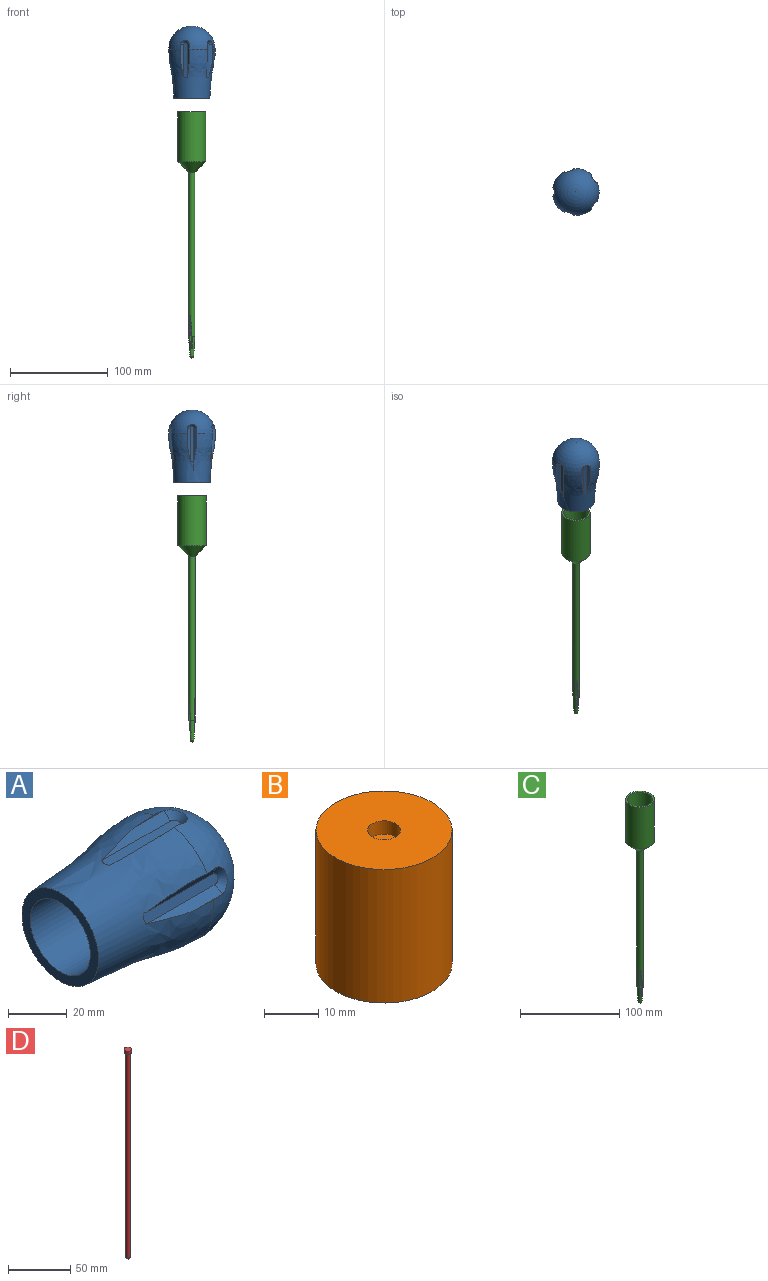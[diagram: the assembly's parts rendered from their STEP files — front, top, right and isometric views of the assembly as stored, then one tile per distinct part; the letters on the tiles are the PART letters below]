
ASSEMBLY  parts=4 mates=3
PART A: 37 faces, bbox 74.1x48.1x48.1 mm
  f0: sphere r=24mm, area 3201.7mm2, adj f1,f6,f7,f8,f9,f10,f12,f13
  f1: revolved ~50x47.78mm, area 5491.9mm2, adj f0,f2,f5,f6,f7,f8,f10,f11
  f2: plane 37x37mm, normal (-1,0,0), area 414.7mm2, adj f1,f3
  f3: cylinder r=14.5mm len=50mm, axis (1,0,0), area 4555.3mm2, adj f2,f4
  f4: plane 29x29mm, normal (-1,0,0), area 169.6mm2, adj f3,f35
  f5: plane 35.69x4.01mm, normal (0,0,1), area 140.2mm2, adj f1,f8,f9,f10
  f6: plane 14.59x0.53mm, normal (0,-1,0), area 4.7mm2, adj f0,f1,f8
  f7: plane 14.59x0.53mm, normal (0,1,0), area 4.7mm2, adj f0,f1,f10
  f8: plane 33.04x3mm, normal (0,-0.71,0.71), area 103.7mm2, adj f0,f1,f5,f6,f9
  f9: cone r=5mm half-angle=45deg, axis (0,0,1), area 35.1mm2, adj f0,f5,f8,f10
  f10: plane 33.04x3mm, normal (0,0.71,0.71), area 103.7mm2, adj f0,f1,f5,f7,f9
  f11: plane 35.69x3.81mm, normal (0,-0.95,0.31), area 140.2mm2, adj f1,f14,f15,f16
  f12: plane 14.59x0.5mm, normal (0,-0.31,-0.95), area 4.7mm2, adj f0,f1,f14
  f13: plane 14.59x0.5mm, normal (0,0.31,0.95), area 4.7mm2, adj f0,f1,f16
  f14: plane 33.04x3.78mm, normal (0,-0.89,-0.45), area 103.7mm2, adj f0,f1,f11,f12,f15
  f15: cone r=5mm half-angle=45deg, axis (0,-0.95,0.31), area 35.1mm2, adj f0,f11,f14,f16
  f16: plane 33.04x3.78mm, normal (0,-0.45,0.89), area 103.7mm2, adj f0,f1,f11,f13,f15
  f17: plane 35.69x3.24mm, normal (0,-0.59,-0.81), area 140.2mm2, adj f1,f20,f21,f22
  f18: plane 14.59x0.44mm, normal (0,0.81,-0.59), area 4.7mm2, adj f0,f1,f20
  f19: plane 14.59x0.44mm, normal (0,-0.81,0.59), area 4.7mm2, adj f0,f1,f22
  f20: plane 33.04x4.19mm, normal (0,0.16,-0.99), area 103.7mm2, adj f0,f1,f17,f18,f21
  f21: cone r=5mm half-angle=45deg, axis (0,-0.59,-0.81), area 35.1mm2, adj f0,f17,f20,f22
  f22: plane 33.04x4.19mm, normal (0,-0.99,-0.16), area 103.7mm2, adj f0,f1,f17,f19,f21
  f23: plane 35.69x3.24mm, normal (0,0.59,-0.81), area 140.2mm2, adj f1,f26,f27,f28
  f24: plane 14.59x0.44mm, normal (0,0.81,0.59), area 4.7mm2, adj f0,f1,f26
  f25: plane 14.59x0.44mm, normal (0,-0.81,-0.59), area 4.7mm2, adj f0,f1,f28
  f26: plane 33.04x4.19mm, normal (0,0.99,-0.16), area 103.7mm2, adj f0,f1,f23,f24,f27
  f27: cone r=5mm half-angle=45deg, axis (0,0.59,-0.81), area 35.1mm2, adj f0,f23,f26,f28
  f28: plane 33.04x4.19mm, normal (0,-0.16,-0.99), area 103.7mm2, adj f0,f1,f23,f25,f27
  f29: plane 35.69x3.81mm, normal (0,0.95,0.31), area 140.2mm2, adj f1,f32,f33,f34
  f30: plane 14.59x0.5mm, normal (0,-0.31,0.95), area 4.7mm2, adj f0,f1,f32
  f31: plane 14.59x0.5mm, normal (0,0.31,-0.95), area 4.7mm2, adj f0,f1,f34
  f32: plane 33.04x3.78mm, normal (0,0.45,0.89), area 103.7mm2, adj f0,f1,f29,f30,f33
  f33: cone r=5mm half-angle=45deg, axis (0,0.95,0.31), area 35.1mm2, adj f0,f29,f32,f34
  f34: plane 33.04x3.78mm, normal (0,0.89,-0.45), area 103.7mm2, adj f0,f1,f29,f31,f33
  f35: cylinder r=12.5mm len=25mm, axis (1,0,0), area 1492.3mm2, adj f4,f36
  f36: plane 25x25mm, normal (-1,0,0), area 490.9mm2, adj f35
PART B: 10 faces, bbox 25x25x30 mm
  f0: plane 25x25mm, normal (0,0,-1), area 487.1mm2, adj f1,f5,f6,f7,f8
  f1: cylinder r=12.5mm len=30mm, axis (0,0,-1), area 2356.2mm2, adj f0,f2
  f2: plane 25x25mm, normal (0,0,1), area 462.6mm2, adj f1,f3
  f3: cylinder r=3mm len=6mm, axis (0,0,1), area 56.5mm2, adj f2,f4
  f4: plane 6x6mm, normal (0,0,1), area 28.3mm2, adj f3
  f5: plane 1.93x1mm, normal (0,1,0), area 1.9mm2, adj f0,f6,f8,f9
  f6: plane 1.97x1mm, normal (1,0,0), area 2mm2, adj f0,f5,f7,f9
  f7: plane 1.93x1mm, normal (0,-1,0), area 1.9mm2, adj f0,f6,f8,f9
  f8: plane 1.97x1mm, normal (-1,0,0), area 2mm2, adj f0,f5,f7,f9
  f9: plane 1.97x1.93mm, normal (0,0,-1), area 3.8mm2, adj f5,f6,f7,f8
PART C: 21 faces, bbox 29.1x29.1x250.1 mm
  f0: cylinder r=1.75mm len=201mm, axis (0,0,-1), area 2210.1mm2, adj f3,f18
  f1: cylinder r=3.25mm len=168mm, axis (0,0,-1), area 3293.7mm2, adj f2,f4,f5,f7,f8,f9,f11,f12
  f2: cone r=3.25mm half-angle=3.7deg, axis (0,0,1), area 249.2mm2, adj f1,f3,f5,f6,f7,f9,f10,f11
  f3: plane 3.9x3.9mm, normal (0,0,-1), area 2.3mm2, adj f0,f2
  f4: plane 1.23x0.89mm, normal (-0.82,0,-0.58), area 0.1mm2, adj f1,f5,f7
  f5: plane 35.17x2.41mm, normal (0,-1,0), area 36.8mm2, adj f1,f2,f4,f6,f7
  f6: plane 1.22x0.62mm, normal (-0.45,0,0.89), area 0.2mm2, adj f2,f5,f7
  f7: plane 34.48x2.49mm, normal (-0.71,-0.71,-0.05), area 38.6mm2, adj f1,f2,f4,f5,f6
  f8: plane 1.23x1.09mm, normal (0.41,-0.71,-0.58), area 0.1mm2, adj f1,f9,f11
  f9: plane 35.2x2.11mm, normal (0.87,0.5,0), area 36.8mm2, adj f1,f2,f8,f10,f11
  f10: plane 1.17x0.62mm, normal (0.22,-0.39,0.89), area 0.2mm2, adj f2,f9,f11
  f11: plane 34.48x2.65mm, normal (0.97,-0.26,-0.05), area 38.6mm2, adj f1,f2,f8,f9,f10
  f12: plane 1.23x1.02mm, normal (0.41,0.71,-0.58), area 0.1mm2, adj f1,f13,f15
  f13: plane 35.17x2.08mm, normal (-0.87,0.5,0), area 36.8mm2, adj f1,f2,f12,f14,f15
  f14: plane 0.96x0.81mm, normal (0.22,0.39,0.89), area 0.2mm2, adj f2,f13,f15
  f15: plane 34.48x2.1mm, normal (-0.26,0.96,-0.05), area 38.6mm2, adj f1,f2,f12,f13,f14
  f16: cylinder r=14.5mm len=50.75mm, axis (0,0,-1), area 4623.6mm2, adj f17,f20
  f17: plane 29x29mm, normal (0,0,1), area 169.6mm2, adj f16,f19
  f18: plane 25x25mm, normal (0,0,1), area 481.3mm2, adj f0,f19
  f19: cylinder r=12.5mm len=49mm, axis (0,0,1), area 3848.5mm2, adj f17,f18
  f20: cone r=15.25mm half-angle=45deg, axis (0,0,1), area 887.2mm2, adj f1,f16
PART D: 5 faces, bbox 6x6x206 mm
  f0: cylinder r=1.75mm len=201.25mm, axis (0,0,-1), area 2212.9mm2, adj f3,f4
  f1: cylinder r=3mm len=6mm, axis (0,0,-1), area 56.5mm2, adj f2,f3
  f2: plane 6x6mm, normal (0,0,1), area 28.3mm2, adj f1
  f3: plane 6x6mm, normal (0,0,-1), area 18.7mm2, adj f0,f1
  f4: sphere r=1.75mm, area 19.2mm2, adj f0
PLACE A rot(axis=(0,-1,0),90deg) t=(0,0,303.96)mm
PLACE B rot(axis=(1,0,0),180deg) t=(0,0,231)mm
PLACE C at identity fixed
PLACE D t=(0,0,-1.84)mm
MATE slider B.f1 <-> C.f19  axis (0,0,-1) through (0,0,201)mm
MATE slider D.f0 <-> C.f19  axis (0,0,-1) through (0,0,201.16)mm
MATE slider C.f16 <-> A.f3  axis (0,0,1) through (0,0,250)mm
